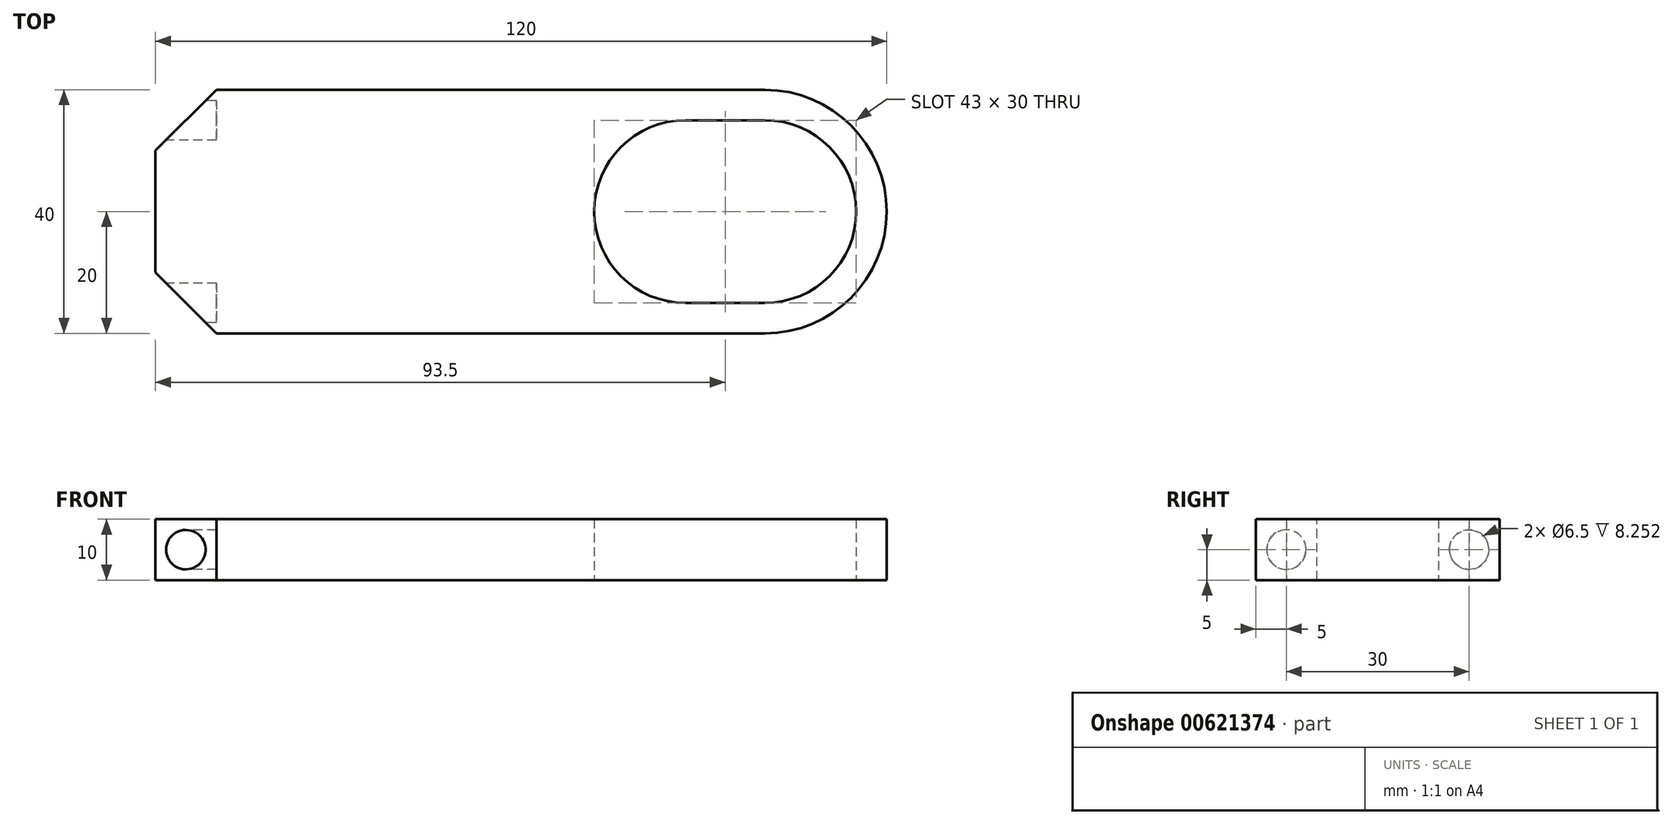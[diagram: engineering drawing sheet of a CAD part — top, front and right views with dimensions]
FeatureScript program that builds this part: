
annotation { "Feature Type Name" : "Feature", "Feature Type Description" : "" }
export const myFeature = defineFeature(function(context is Context, id is Id, definition is map)
    precondition{}
    {
        {
            var Q0;
            Q0=qCreatedBy(makeId("Top.planeOp"),FACE);
            var sketch = newSketch(context, id + "F0", { "sketchPlane" : qUnion([Q0])});
            skLineSegment(sketch, "E0", {"start": v(20, -15) * mm, "end": v(7, -15) * mm});
            skArc(sketch, "E1", {"start": v(7, 15) * mm, "mid": v(-8, 0) * mm, "end": v(7, -15) * mm});
            skLineSegment(sketch, "E2", {"start": v(7, 15) * mm, "end": v(20, 15) * mm});
            skArc(sketch, "E3", {"start": v(20, -15) * mm, "mid": v(35, 0) * mm, "end": v(20, 15) * mm});
            skLineSegment(sketch, "E4", {"start": v(-80, 20) * mm, "end": v(20, 20) * mm});
            skLineSegment(sketch, "E5", {"start": v(-80, 20) * mm, "end": v(-80, -20) * mm});
            skLineSegment(sketch, "E6.MirrorCS", {"start": v(-80, -20) * mm, "end": v(20, -20) * mm});
            skArc(sketch, "E7", {"start": v(20, -20) * mm, "mid": v(40, 0) * mm, "end": v(20, 20) * mm});
            skLineSegment(sketch, "E8", {"start": v(-64.46, 20) * mm, "end": v(-64.46, -20) * mm, "construction": true});
            skLineSegment(sketch, "E9", {"start": v(-64.46, 0) * mm, "end": v(59.85, 0) * mm, "construction": true});
            skLineSegment(sketch, "E10", {"start": v(14.02, 0) * mm, "end": v(14.02, 6.03) * mm});
            skLineSegment(sketch, "E11", {"start": v(14.02, 6.03) * mm, "end": v(14.02, -5.37) * mm, "construction": true});
            skLineSegment(sketch, "E12", {"start": v(-64.46, 0) * mm, "end": v(14.02, -5.37) * mm, "construction": true});
            skLineSegment(sketch, "E13", {"start": v(14.02, 6.03) * mm, "end": v(-64.46, 0) * mm, "construction": true});
            skSolve(sketch);
        }
        {
            var Q0;
            Q0 = qSketchRegion(id + "F0", true);
            extrude(context, id + "F1", {"entities" : qUnion([Q0]), "depth" : 10 * mm, "offsetDistance" : 25 * mm});
        }
        {
            var Q0;
            Q0=makeQuery(id+"F1.opExtrude","SWEPT_FACE",FACE,{"disambiguationData":[OSD([sQuery(id+"F0.wireOp",EDGE,"E5")])]});
            var sketch = newSketch(context, id + "F2", { "sketchPlane" : qUnion([Q0])});
            skCircle(sketch, "E14", {"center": v(-15, 5) * mm, "radius": 3.25 * mm});
            skCircle(sketch, "E15.MirrorC", {"center": v(15, 5) * mm, "radius": 3.25 * mm});
            skSolve(sketch);
        }
        {
            var Q0;
            Q0 = qSketchRegion(id + "F2", true);
            extrude(context, id + "F3", {"entities" : qUnion([Q0]), "operationType" : NewBodyOperationType.REMOVE, "oppositeDirection" : true, "depth" : 10 * mm, "offsetDistance" : 25 * mm});
        }
        {
            var Q0;
            Q0=makeQuery(id+"F1.opExtrude","SWEPT_EDGE",EDGE,{"disambiguationData":[OSD([sQuery(id+"F0.wireOp",EDGE,"E4"),sQuery(id+"F0.wireOp",EDGE,"E5")])]});
            var Q1;
            Q1=makeQuery(id+"F1.opExtrude","SWEPT_EDGE",EDGE,{"disambiguationData":[OSD([sQuery(id+"F0.wireOp",EDGE,"E5"),sQuery(id+"F0.wireOp",EDGE,"E6.MirrorCS")])]});
            chamfer(context, id + "F4", {"entities" : qUnion([Q0, Q1]), "width" : 10 * mm, "tangentPropagation" : true});
        }
    });
